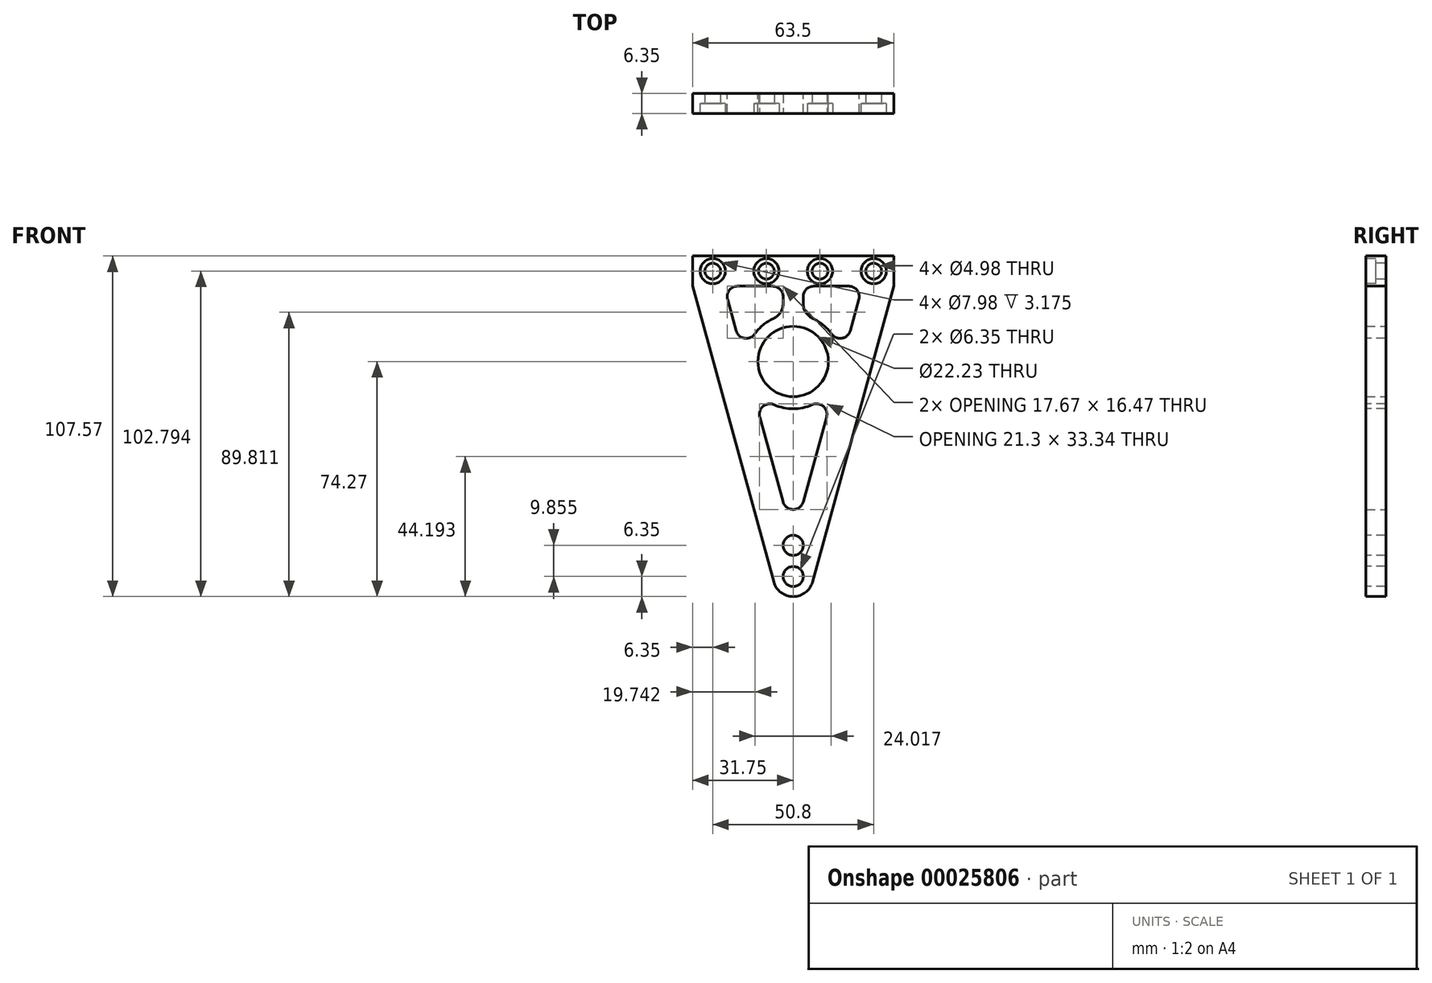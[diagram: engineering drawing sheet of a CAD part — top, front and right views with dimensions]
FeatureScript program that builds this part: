
annotation { "Feature Type Name" : "Feature", "Feature Type Description" : "" }
export const myFeature = defineFeature(function(context is Context, id is Id, definition is map)
    precondition{}
    {
        {
            var Q0;
            Q0=qCreatedBy(makeId("Front.planeOp"),FACE);
            var sketch = newSketch(context, id + "F0", { "sketchPlane" : qUnion([Q0])});
            skCircle(sketch, "E0", {"center": v(0, 0) * mm, "radius": 11.11 * mm});
            skLineSegment(sketch, "E1", {"start": v(0, 0) * mm, "end": v(0, 38.71) * mm, "construction": true});
            skLineSegment(sketch, "E2", {"start": v(0, 0) * mm, "end": v(56.24, 0) * mm, "construction": true});
            skLineSegment(sketch, "E3", {"start": v(0, 33.3) * mm, "end": v(31.75, 33.3) * mm});
            skLineSegment(sketch, "E4", {"start": v(31.75, 33.3) * mm, "end": v(31.75, 23.77) * mm});
            skLineSegment(sketch, "E5", {"start": v(31.75, 23.77) * mm, "end": v(6.12, -69.6) * mm});
            skLineSegment(sketch, "E6", {"start": v(-6.12, -69.6) * mm, "end": v(-31.75, 23.77) * mm});
            skLineSegment(sketch, "E7", {"start": v(-31.75, 23.77) * mm, "end": v(-31.75, 33.3) * mm});
            skLineSegment(sketch, "E8", {"start": v(-31.75, 33.3) * mm, "end": v(0, 33.3) * mm});
            skArc(sketch, "E9", {"start": v(-6.12, -69.6) * mm, "mid": v(0, -74.27) * mm, "end": v(6.12, -69.6) * mm});
            skPoint(sketch, "E10", {"position": v(0, -74.27) * mm});
            skLineSegment(sketch, "E11", {"start": v(-49.73, 28.52) * mm, "end": v(49.74, 28.52) * mm, "construction": true});
            skPoint(sketch, "E12", {"position": v(-25.4, 28.52) * mm});
            skPoint(sketch, "E13", {"position": v(-8.46, 28.52) * mm});
            skPoint(sketch, "E14", {"position": v(8.46, 28.52) * mm});
            skPoint(sketch, "E15", {"position": v(25.4, 28.52) * mm});
            skSolve(sketch);
        }
        {
            var Q0;
            Q0=makeQuery(id+"F0.imprint","IMPRINT",FACE,{"disambiguationData":[TD([[makeQuery(id+"F0.imprint","IMPRINT",EDGE,{"derivedFrom":sQuery(id+"F0.wireOp",EDGE,"E0")}),-1.0]])]});
            extrude(context, id + "F1", {"entities" : qUnion([Q0]), "depth" : 6.35 * mm});
        }
        {
            var Q0;
            Q0=makeQuery(id+"F1.opExtrude","CAP_FACE",FACE,{"disambiguationData":[OSD([sQuery(id+"F0.wireOp",EDGE,"E0"),sQuery(id+"F0.wireOp",EDGE,"E3"),sQuery(id+"F0.wireOp",EDGE,"E4"),sQuery(id+"F0.wireOp",EDGE,"E5"),sQuery(id+"F0.wireOp",EDGE,"E6"),sQuery(id+"F0.wireOp",EDGE,"E7"),sQuery(id+"F0.wireOp",EDGE,"E8"),sQuery(id+"F0.wireOp",EDGE,"E9")])],"isStart":false});
            var sketch = newSketch(context, id + "F2", { "sketchPlane" : qUnion([Q0])});
            skLineSegment(sketch, "E16.0", {"start": v(21.87, 23.77) * mm, "end": v(3.18, 23.77) * mm});
            skLineSegment(sketch, "E16.2", {"start": v(0, -55.92) * mm, "end": v(13.77, -5.75) * mm});
            skLineSegment(sketch, "E16.3", {"start": v(-21.87, 23.77) * mm, "end": v(-14.78, -2.08) * mm});
            skArc(sketch, "E17", {"start": v(14.78, -2.08) * mm, "mid": v(12.25, 8.53) * mm, "end": v(3.18, 14.58) * mm});
            skArc(sketch, "E18.trimOffspring", {"start": v(-13.77, -5.75) * mm, "mid": v(0, -14.92) * mm, "end": v(13.77, -5.75) * mm});
            skLineSegment(sketch, "E19.trimOffspring", {"start": v(-13.77, -5.75) * mm, "end": v(0, -55.92) * mm});
            skLineSegment(sketch, "E20.trimOffspring", {"start": v(14.78, -2.08) * mm, "end": v(21.87, 23.77) * mm});
            skLineSegment(sketch, "E21", {"start": v(0, 0) * mm, "end": v(0, 60.06) * mm, "construction": true});
            skLineSegment(sketch, "E22", {"start": v(-3.18, 14.58) * mm, "end": v(-3.18, 23.77) * mm});
            skLineSegment(sketch, "E23", {"start": v(3.18, 14.58) * mm, "end": v(3.18, 23.77) * mm});
            skLineSegment(sketch, "E24.trimOffspring", {"start": v(-3.17, 23.77) * mm, "end": v(-21.87, 23.77) * mm});
            skArc(sketch, "E25.trimOffspring", {"start": v(-3.18, 14.58) * mm, "mid": v(-12.25, 8.53) * mm, "end": v(-14.78, -2.08) * mm});
            skSolve(sketch);
        }
        {
            var Q0;
            Q0=makeQuery(id+"F2.imprint","IMPRINT",FACE,{"disambiguationData":[TD([[makeQuery(id+"F2.imprint","IMPRINT",EDGE,{"derivedFrom":sQuery(id+"F2.wireOp",EDGE,"E16.3")}),1.0]])]});
            var Q1;
            Q1=makeQuery(id+"F2.imprint","IMPRINT",FACE,{"disambiguationData":[TD([[makeQuery(id+"F2.imprint","IMPRINT",EDGE,{"derivedFrom":sQuery(id+"F2.wireOp",EDGE,"E16.0")}),1.0]])]});
            var Q2;
            Q2=makeQuery(id+"F2.imprint","IMPRINT",FACE,{"disambiguationData":[TD([[makeQuery(id+"F2.imprint","IMPRINT",EDGE,{"derivedFrom":sQuery(id+"F2.wireOp",EDGE,"E16.2")}),1.0]])]});
            extrude(context, id + "F3", {"entities" : qUnion([Q0, Q1, Q2]), "operationType" : NewBodyOperationType.REMOVE, "oppositeDirection" : true, "depth" : 25.4 * mm});
        }
        {
            var Q0;
            Q0=makeQuery(id+"F3.boolean.opBoolean","COPY",EDGE,{"derivedFrom":makeQuery(id+"F3.opExtrude","SWEPT_EDGE",EDGE,{"disambiguationData":[OSD([sQuery(id+"F2.wireOp",EDGE,"E16.3"),sQuery(id+"F2.wireOp",EDGE,"E24.trimOffspring")])]})});
            var Q1;
            Q1=makeQuery(id+"F3.boolean.opBoolean","COPY",EDGE,{"derivedFrom":makeQuery(id+"F3.opExtrude","SWEPT_EDGE",EDGE,{"disambiguationData":[OSD([sQuery(id+"F2.wireOp",EDGE,"E22"),sQuery(id+"F2.wireOp",EDGE,"E24.trimOffspring")])]})});
            var Q2;
            Q2=makeQuery(id+"F3.boolean.opBoolean","COPY",EDGE,{"derivedFrom":makeQuery(id+"F3.opExtrude","SWEPT_EDGE",EDGE,{"disambiguationData":[OSD([sQuery(id+"F2.wireOp",EDGE,"E16.0"),sQuery(id+"F2.wireOp",EDGE,"E20.trimOffspring")])]})});
            var Q3;
            Q3=makeQuery(id+"F3.boolean.opBoolean","COPY",EDGE,{"derivedFrom":makeQuery(id+"F3.opExtrude","SWEPT_EDGE",EDGE,{"disambiguationData":[OSD([sQuery(id+"F2.wireOp",EDGE,"E16.0"),sQuery(id+"F2.wireOp",EDGE,"E23")])]})});
            var Q4;
            Q4=makeQuery(id+"F3.boolean.opBoolean","COPY",EDGE,{"derivedFrom":makeQuery(id+"F3.opExtrude","SWEPT_EDGE",EDGE,{"disambiguationData":[OSD([sQuery(id+"F2.wireOp",EDGE,"E16.2"),sQuery(id+"F2.wireOp",EDGE,"E19.trimOffspring")])]})});
            fillet(context, id + "F4", {"entities" : qUnion([Q0, Q1, Q2, Q3, Q4]), "radius" : 3.3 * mm, "tangentPropagation" : true, "allowEdgeOverflow" : false});
        }
        {
            var Q0;
            Q0=makeQuery(id+"F3.boolean.opBoolean","COPY",EDGE,{"derivedFrom":makeQuery(id+"F3.opExtrude","SWEPT_EDGE",EDGE,{"disambiguationData":[OSD([sQuery(id+"F2.wireOp",EDGE,"E22"),sQuery(id+"F2.wireOp",EDGE,"E25.trimOffspring")])]})});
            var Q1;
            Q1=makeQuery(id+"F3.boolean.opBoolean","COPY",EDGE,{"derivedFrom":makeQuery(id+"F3.opExtrude","SWEPT_EDGE",EDGE,{"disambiguationData":[OSD([sQuery(id+"F2.wireOp",EDGE,"E17"),sQuery(id+"F2.wireOp",EDGE,"E23")])]})});
            fillet(context, id + "F5", {"entities" : qUnion([Q0, Q1]), "radius" : 5.08 * mm, "tangentPropagation" : true, "allowEdgeOverflow" : false});
        }
        {
            var Q0;
            Q0=makeQuery(id+"F3.boolean.opBoolean","COPY",EDGE,{"derivedFrom":makeQuery(id+"F3.opExtrude","SWEPT_EDGE",EDGE,{"disambiguationData":[OSD([sQuery(id+"F2.wireOp",EDGE,"E16.3"),sQuery(id+"F2.wireOp",EDGE,"E25.trimOffspring")])]})});
            var Q1;
            Q1=makeQuery(id+"F3.boolean.opBoolean","COPY",EDGE,{"derivedFrom":makeQuery(id+"F3.opExtrude","SWEPT_EDGE",EDGE,{"disambiguationData":[OSD([sQuery(id+"F2.wireOp",EDGE,"E16.2"),sQuery(id+"F2.wireOp",EDGE,"E18.trimOffspring")])]})});
            var Q2;
            Q2=makeQuery(id+"F3.boolean.opBoolean","COPY",EDGE,{"derivedFrom":makeQuery(id+"F3.opExtrude","SWEPT_EDGE",EDGE,{"disambiguationData":[OSD([sQuery(id+"F2.wireOp",EDGE,"E18.trimOffspring"),sQuery(id+"F2.wireOp",EDGE,"E19.trimOffspring")])]})});
            var Q3;
            Q3=makeQuery(id+"F3.boolean.opBoolean","COPY",EDGE,{"derivedFrom":makeQuery(id+"F3.opExtrude","SWEPT_EDGE",EDGE,{"disambiguationData":[OSD([sQuery(id+"F2.wireOp",EDGE,"E17"),sQuery(id+"F2.wireOp",EDGE,"E20.trimOffspring")])]})});
            fillet(context, id + "F6", {"entities" : qUnion([Q0, Q1, Q2, Q3]), "radius" : 3.3 * mm, "tangentPropagation" : true, "allowEdgeOverflow" : false});
        }
        {
            var Q0;
            Q0=makeQuery(id+"F1.opExtrude","CAP_FACE",FACE,{"disambiguationData":[OSD([sQuery(id+"F0.wireOp",EDGE,"E0"),sQuery(id+"F0.wireOp",EDGE,"E3"),sQuery(id+"F0.wireOp",EDGE,"E4"),sQuery(id+"F0.wireOp",EDGE,"E5"),sQuery(id+"F0.wireOp",EDGE,"E6"),sQuery(id+"F0.wireOp",EDGE,"E7"),sQuery(id+"F0.wireOp",EDGE,"E8"),sQuery(id+"F0.wireOp",EDGE,"E9")])],"isStart":false});
            var sketch = newSketch(context, id + "F7", { "sketchPlane" : qUnion([Q0])});
            skLineSegment(sketch, "E26", {"start": v(-39.8, 28.52) * mm, "end": v(45.62, 28.52) * mm});
            skPoint(sketch, "E27", {"position": v(-25.4, 28.52) * mm});
            skPoint(sketch, "E28", {"position": v(-8.46, 28.52) * mm});
            skPoint(sketch, "E29", {"position": v(8.46, 28.52) * mm});
            skPoint(sketch, "E30", {"position": v(25.4, 28.52) * mm});
            skLineSegment(sketch, "E31", {"start": v(0, 28.52) * mm, "end": v(0, -114.68) * mm});
            skSolve(sketch);
        }
        {
            var Q0;
            Q0=sQuery(id+"F7.wireOp",VERTEX,"E27");
            var Q1;
            Q1=sQuery(id+"F7.wireOp",VERTEX,"E28");
            var Q2;
            Q2=sQuery(id+"F7.wireOp",VERTEX,"E29");
            var Q3;
            Q3=sQuery(id+"F7.wireOp",VERTEX,"E30");
            var Q4;
            Q4=makeQuery(id+"F1.opExtrude","SWEPT_BODY",BODY,{"disambiguationData":[OSD([sQuery(id+"F0.wireOp",EDGE,"E0"),sQuery(id+"F0.wireOp",EDGE,"E3"),sQuery(id+"F0.wireOp",EDGE,"E4"),sQuery(id+"F0.wireOp",EDGE,"E5"),sQuery(id+"F0.wireOp",EDGE,"E6"),sQuery(id+"F0.wireOp",EDGE,"E7"),sQuery(id+"F0.wireOp",EDGE,"E8"),sQuery(id+"F0.wireOp",EDGE,"E9")])]});
            hole(context, id + "F8", {"style" : HoleStyle.C_BORE, "holeDiameter" : 4.98 * mm, "cBoreDiameter" : 7.98 * mm, "cBoreDepth" : 3.17 * mm, "endStyle" : HoleEndStyle.THROUGH, "locations" : qUnion([Q0, Q1, Q2, Q3]), "scope" : qUnion([Q4])});
        }
        {
            var Q0;
            Q0=makeQuery(id+"F1.opExtrude","CAP_FACE",FACE,{"disambiguationData":[OSD([sQuery(id+"F0.wireOp",EDGE,"E0"),sQuery(id+"F0.wireOp",EDGE,"E3"),sQuery(id+"F0.wireOp",EDGE,"E4"),sQuery(id+"F0.wireOp",EDGE,"E5"),sQuery(id+"F0.wireOp",EDGE,"E6"),sQuery(id+"F0.wireOp",EDGE,"E7"),sQuery(id+"F0.wireOp",EDGE,"E8"),sQuery(id+"F0.wireOp",EDGE,"E9")])],"isStart":false});
            var sketch = newSketch(context, id + "F9", { "sketchPlane" : qUnion([Q0])});
            skLineSegment(sketch, "E32", {"start": v(0, 44.3) * mm, "end": v(0, -86.28) * mm});
            skPoint(sketch, "E33", {"position": v(0, -58.06) * mm});
            skPoint(sketch, "E34", {"position": v(0, -67.92) * mm});
            skSolve(sketch);
        }
        {
            var Q0;
            Q0=sQuery(id+"F9.wireOp",VERTEX,"E33");
            var Q1;
            Q1=sQuery(id+"F9.wireOp",VERTEX,"E34");
            var Q2;
            Q2=makeQuery(id+"F1.opExtrude","SWEPT_BODY",BODY,{"disambiguationData":[OSD([sQuery(id+"F0.wireOp",EDGE,"E0"),sQuery(id+"F0.wireOp",EDGE,"E3"),sQuery(id+"F0.wireOp",EDGE,"E4"),sQuery(id+"F0.wireOp",EDGE,"E5"),sQuery(id+"F0.wireOp",EDGE,"E6"),sQuery(id+"F0.wireOp",EDGE,"E7"),sQuery(id+"F0.wireOp",EDGE,"E8"),sQuery(id+"F0.wireOp",EDGE,"E9")])]});
            hole(context, id + "F10", {"style" : HoleStyle.SIMPLE, "holeDiameter" : 6.35 * mm, "endStyle" : HoleEndStyle.THROUGH, "locations" : qUnion([Q0, Q1]), "scope" : qUnion([Q2])});
        }
    });
